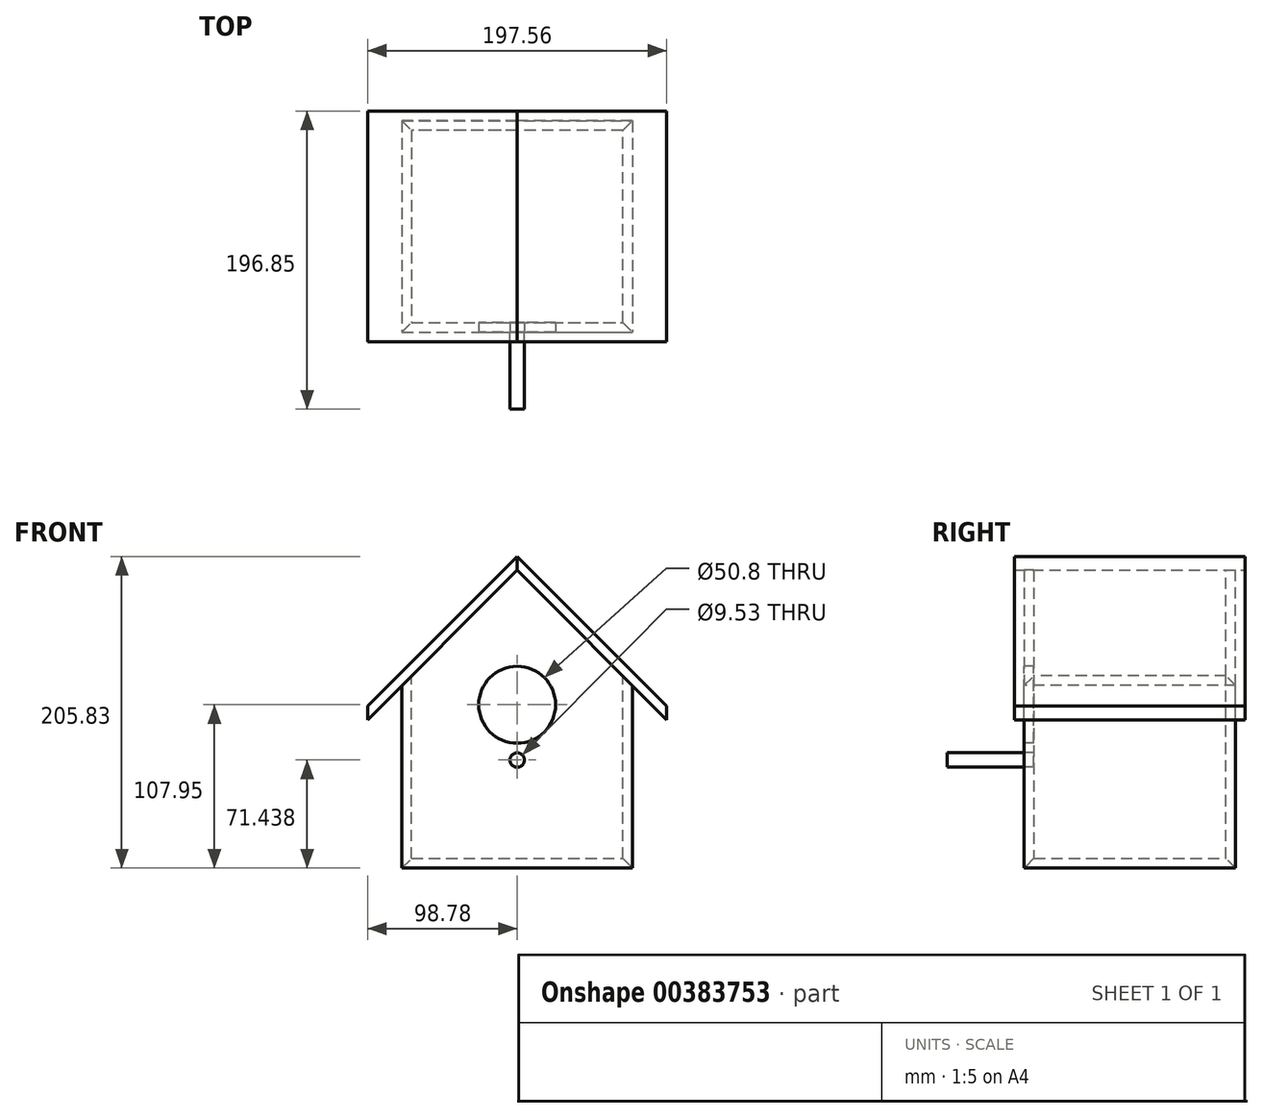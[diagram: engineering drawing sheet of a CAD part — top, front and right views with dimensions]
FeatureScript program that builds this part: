
annotation { "Feature Type Name" : "Feature", "Feature Type Description" : "" }
export const myFeature = defineFeature(function(context is Context, id is Id, definition is map)
    precondition{}
    {
        {
            var Q0;
            Q0=qCreatedBy(makeId("Front.planeOp"),FACE);
            var sketch = newSketch(context, id + "F0", { "sketchPlane" : qUnion([Q0])});
            skLineSegment(sketch, "E0.bottom", {"start": v(-76.2, 0) * mm, "end": v(76.2, 0) * mm});
            skLineSegment(sketch, "E0.top", {"start": v(-76.2, 6.35) * mm, "end": v(76.2, 6.35) * mm});
            skLineSegment(sketch, "E0.left", {"start": v(-76.2, 0) * mm, "end": v(-76.2, 6.35) * mm});
            skLineSegment(sketch, "E0.right", {"start": v(76.2, 0) * mm, "end": v(76.2, 6.35) * mm});
            skPoint(sketch, "E0.middle", {"position": v(0, 3.17) * mm});
            skSolve(sketch);
        }
        {
            var Q0;
            Q0 = qSketchRegion(id + "F0", true);
            extrude(context, id + "F1", {"entities" : qUnion([Q0]), "oppositeDirection" : true, "depth" : 139.7 * mm});
        }
        {
            var Q0;
            Q0=makeQuery(id+"F1.opExtrude","SWEPT_FACE",FACE,{"disambiguationData":[OSD([sQuery(id+"F0.wireOp",EDGE,"E0.top")])]});
            chamfer(context, id + "F2", {"entities" : qUnion([Q0]), "chamferType" : ChamferType.OFFSET_ANGLE, "width" : 6.35 * mm, "oppositeDirection" : false, "angle" : 45 * degree, "tangentPropagation" : true});
        }
        {
            var Q0;
            Q0=qCreatedBy(makeId("Front.planeOp"),FACE);
            var sketch = newSketch(context, id + "F3", { "sketchPlane" : qUnion([Q0])});
            skLineSegment(sketch, "E1.bottom", {"start": v(-76.2, 0) * mm, "end": v(-69.85, 0) * mm});
            skLineSegment(sketch, "E1.top", {"start": v(-76.2, 127) * mm, "end": v(-69.85, 127) * mm});
            skLineSegment(sketch, "E1.left", {"start": v(-76.2, 0) * mm, "end": v(-76.2, 127) * mm});
            skLineSegment(sketch, "E1.right", {"start": v(-69.85, 0) * mm, "end": v(-69.85, 127) * mm});
            skLineSegment(sketch, "E2.bottom", {"start": v(76.2, 0) * mm, "end": v(69.85, 0) * mm});
            skLineSegment(sketch, "E2.top", {"start": v(76.2, 127) * mm, "end": v(69.85, 127) * mm});
            skLineSegment(sketch, "E2.left", {"start": v(76.2, 0) * mm, "end": v(76.2, 127) * mm});
            skLineSegment(sketch, "E2.right", {"start": v(69.85, 0) * mm, "end": v(69.85, 127) * mm});
            skSolve(sketch);
        }
        {
            var Q0;
            Q0 = qSketchRegion(id + "F3", true);
            extrude(context, id + "F4", {"entities" : qUnion([Q0]), "oppositeDirection" : true, "depth" : 139.7 * mm});
        }
        {
            var Q0;
            Q0=makeQuery(id+"F4.opExtrude","CAP_EDGE",EDGE,{"disambiguationData":[OSD([sQuery(id+"F3.wireOp",EDGE,"E1.right")])],"isStart":false});
            var Q1;
            Q1=makeQuery(id+"F4.opExtrude","SWEPT_EDGE",EDGE,{"disambiguationData":[OSD([sQuery(id+"F3.wireOp",EDGE,"E1.bottom"),sQuery(id+"F3.wireOp",EDGE,"E1.right")])]});
            var Q2;
            Q2=makeQuery(id+"F4.opExtrude","CAP_EDGE",EDGE,{"disambiguationData":[OSD([sQuery(id+"F3.wireOp",EDGE,"E1.right")])],"isStart":true});
            var Q3;
            Q3=makeQuery(id+"F4.opExtrude","CAP_EDGE",EDGE,{"disambiguationData":[OSD([sQuery(id+"F3.wireOp",EDGE,"E2.right")])],"isStart":true});
            var Q4;
            Q4=makeQuery(id+"F4.opExtrude","SWEPT_EDGE",EDGE,{"disambiguationData":[OSD([sQuery(id+"F3.wireOp",EDGE,"E2.bottom"),sQuery(id+"F3.wireOp",EDGE,"E2.right")])]});
            var Q5;
            Q5=makeQuery(id+"F4.opExtrude","CAP_EDGE",EDGE,{"disambiguationData":[OSD([sQuery(id+"F3.wireOp",EDGE,"E2.right")])],"isStart":false});
            chamfer(context, id + "F5", {"entities" : qUnion([Q0, Q1, Q2, Q3, Q4, Q5]), "chamferType" : ChamferType.OFFSET_ANGLE, "width" : 6.35 * mm, "oppositeDirection" : false, "angle" : 45 * degree, "tangentPropagation" : true});
        }
        {
            var Q0;
            Q0=qCreatedBy(makeId("Front.planeOp"),FACE);
            cPlane(context, id + "F6", {"entities" : qUnion([Q0]), "cplaneType" : CPlaneType.OFFSET, "offset" : 139.7 * mm, "oppositeDirection" : true, "width" : 152.4 * mm, "height" : 152.4 * mm});
        }
        {
            var Q0;
            Q0=qCreatedBy(makeId("Front.planeOp"),FACE);
            var sketch = newSketch(context, id + "F7", { "sketchPlane" : qUnion([Q0])});
            skLineSegment(sketch, "E3", {"start": v(0, 196.85) * mm, "end": v(76.2, 120.65) * mm});
            skLineSegment(sketch, "E4", {"start": v(76.2, 120.65) * mm, "end": v(76.2, 0) * mm});
            skLineSegment(sketch, "E5", {"start": v(76.2, 0) * mm, "end": v(-76.2, 0) * mm});
            skLineSegment(sketch, "E6", {"start": v(-76.2, 0) * mm, "end": v(-76.2, 120.65) * mm});
            skLineSegment(sketch, "E7", {"start": v(-76.2, 120.65) * mm, "end": v(0, 196.85) * mm});
            skCircle(sketch, "E8", {"center": v(0, 107.95) * mm, "radius": 25.4 * mm});
            skCircle(sketch, "E9", {"center": v(0, 71.44) * mm, "radius": 4.76 * mm});
            skSolve(sketch);
        }
        {
            var Q0;
            Q0 = qSketchRegion(id + "F7", true);
            extrude(context, id + "F8", {"entities" : qUnion([Q0]), "oppositeDirection" : true, "depth" : 6.35 * mm});
        }
        {
            var Q0;
            Q0=qCreatedBy(id+"F6.planeOp",FACE);
            var sketch = newSketch(context, id + "F9", { "sketchPlane" : qUnion([Q0])});
            skLineSegment(sketch, "E10", {"start": v(0, 196.85) * mm, "end": v(-76.2, 120.65) * mm});
            skLineSegment(sketch, "E11", {"start": v(-76.2, 120.65) * mm, "end": v(-76.2, 0) * mm});
            skLineSegment(sketch, "E12", {"start": v(-76.2, 0) * mm, "end": v(76.2, 0) * mm});
            skLineSegment(sketch, "E13", {"start": v(76.2, 0) * mm, "end": v(76.2, 120.65) * mm});
            skLineSegment(sketch, "E14", {"start": v(76.2, 120.65) * mm, "end": v(0, 196.85) * mm});
            skSolve(sketch);
        }
        {
            var Q0;
            Q0 = qSketchRegion(id + "F9", true);
            extrude(context, id + "F10", {"entities" : qUnion([Q0]), "depth" : 6.35 * mm});
        }
        {
            var Q0;
            Q0=makeQuery(id+"F8.opExtrude","CAP_EDGE",EDGE,{"disambiguationData":[OSD([sQuery(id+"F7.wireOp",EDGE,"E4")])],"isStart":false});
            var Q1;
            Q1=makeQuery(id+"F8.opExtrude","CAP_EDGE",EDGE,{"disambiguationData":[OSD([sQuery(id+"F7.wireOp",EDGE,"E5")])],"isStart":false});
            var Q2;
            Q2=makeQuery(id+"F8.opExtrude","CAP_EDGE",EDGE,{"disambiguationData":[OSD([sQuery(id+"F7.wireOp",EDGE,"E6")])],"isStart":false});
            var Q3;
            Q3=makeQuery(id+"F10.opExtrude","CAP_EDGE",EDGE,{"disambiguationData":[OSD([sQuery(id+"F9.wireOp",EDGE,"E11")])],"isStart":false});
            var Q4;
            Q4=makeQuery(id+"F10.opExtrude","CAP_EDGE",EDGE,{"disambiguationData":[OSD([sQuery(id+"F9.wireOp",EDGE,"E12")])],"isStart":false});
            var Q5;
            Q5=makeQuery(id+"F10.opExtrude","CAP_EDGE",EDGE,{"disambiguationData":[OSD([sQuery(id+"F9.wireOp",EDGE,"E13")])],"isStart":false});
            chamfer(context, id + "F11", {"entities" : qUnion([Q0, Q1, Q2, Q3, Q4, Q5]), "chamferType" : ChamferType.OFFSET_ANGLE, "width" : 6.35 * mm, "oppositeDirection" : false, "angle" : 45 * degree, "tangentPropagation" : true});
        }
        {
            var Q0;
            Q0=qCreatedBy(makeId("Front.planeOp"),FACE);
            var sketch = newSketch(context, id + "F12", { "sketchPlane" : qUnion([Q0])});
            skLineSegment(sketch, "E15", {"start": v(0, 196.85) * mm, "end": v(0, 205.83) * mm});
            skLineSegment(sketch, "E16", {"start": v(0, 205.83) * mm, "end": v(-98.78, 107.05) * mm});
            skLineSegment(sketch, "E17", {"start": v(-98.78, 107.05) * mm, "end": v(-98.78, 98.07) * mm});
            skLineSegment(sketch, "E18", {"start": v(-98.78, 98.07) * mm, "end": v(0, 196.85) * mm});
            skSolve(sketch);
        }
        {
            var Q0;
            Q0 = qSketchRegion(id + "F12", true);
            extrude(context, id + "F13", {"entities" : qUnion([Q0]), "depth" : 6.35 * mm, "hasSecondDirection" : true, "secondDirectionOppositeDirection" : true, "secondDirectionDepth" : 146.05 * mm});
        }
        {
            var Q0;
            Q0=makeQuery(id+"F13.opExtrude","SWEPT_BODY",BODY,{"disambiguationData":[OSD([sQuery(id+"F12.wireOp",EDGE,"E15"),sQuery(id+"F12.wireOp",EDGE,"E16"),sQuery(id+"F12.wireOp",EDGE,"E17"),sQuery(id+"F12.wireOp",EDGE,"E18")])]});
            var Q1;
            Q1=qCreatedBy(makeId("Right.planeOp"),FACE);
            mirror(context, id + "F14", {"entities" : qUnion([Q0]), "mirrorPlane" : qUnion([Q1])});
        }
        {
            var Q0;
            Q0=makeQuery(id+"F13.opExtrude","SWEPT_BODY",BODY,{"disambiguationData":[OSD([sQuery(id+"F12.wireOp",EDGE,"E15"),sQuery(id+"F12.wireOp",EDGE,"E16"),sQuery(id+"F12.wireOp",EDGE,"E17"),sQuery(id+"F12.wireOp",EDGE,"E18")])]});
            var Q1;
            Q1=makeQuery(id+"F14.opPattern","COPY",BODY,{"derivedFrom":makeQuery(id+"F13.opExtrude","SWEPT_BODY",BODY,{"disambiguationData":[OSD([sQuery(id+"F12.wireOp",EDGE,"E15"),sQuery(id+"F12.wireOp",EDGE,"E16"),sQuery(id+"F12.wireOp",EDGE,"E17"),sQuery(id+"F12.wireOp",EDGE,"E18")])]}),"instanceName":"1"});
            var Q2;
            Q2=makeQuery(id+"F4.opExtrude","SWEPT_BODY",BODY,{"disambiguationData":[OSD([sQuery(id+"F3.wireOp",EDGE,"E1.bottom"),sQuery(id+"F3.wireOp",EDGE,"E1.top"),sQuery(id+"F3.wireOp",EDGE,"E1.left"),sQuery(id+"F3.wireOp",EDGE,"E1.right")])]});
            var Q3;
            Q3=makeQuery(id+"F4.opExtrude","SWEPT_BODY",BODY,{"disambiguationData":[OSD([sQuery(id+"F3.wireOp",EDGE,"E2.bottom"),sQuery(id+"F3.wireOp",EDGE,"E2.top"),sQuery(id+"F3.wireOp",EDGE,"E2.left"),sQuery(id+"F3.wireOp",EDGE,"E2.right")])]});
            booleanBodies(context, id + "F15", {"operationType" : BooleanOperationType.SUBTRACTION, "tools" : qUnion([Q0, Q1]), "targets" : qUnion([Q2, Q3]), "keepTools" : true});
        }
        {
            var Q0;
            Q0=makeQuery(id+"F7.imprint","IMPRINT",FACE,{"disambiguationData":[TD([[makeQuery(id+"F7.imprint","IMPRINT",EDGE,{"derivedFrom":sQuery(id+"F7.wireOp",EDGE,"E9")}),1.0]])]});
            extrude(context, id + "F16", {"entities" : qUnion([Q0]), "depth" : 50.8 * mm});
        }
    });
